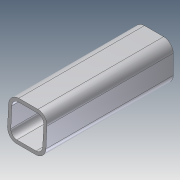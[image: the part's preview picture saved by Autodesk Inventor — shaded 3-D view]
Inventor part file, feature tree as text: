
AUTODESK INVENTOR PART (.ipt)
format: ipt  version: unknown  size: 195,072 bytes
history: native  units: in
note: dims shown in document units (in); Inventor stores cm internally (conversion verified against a paired STEP export)
features: extrude x2, sketch x2
ambient origin geometry x8: Origin, YZ Plane, XZ Plane, XY Plane, X Axis, Y Axis, Z Axis, Center Point
bodies: Solid1 (feature_tree)
feature tree (4):
  extrude  "Extrusion1"  Depth=0.375in
  extrude  "Extrusion2"  Depth=5.0in TaperAngle=0.0deg
  sketch  "Sketch1"  dims[d0=1.5in d1=0.375in]
  sketch  "Sketch2"  dims[d2=0.125in d3=5.0in d4=0.0in d5=0.0206in d6=6.656in d7=0.0in]
